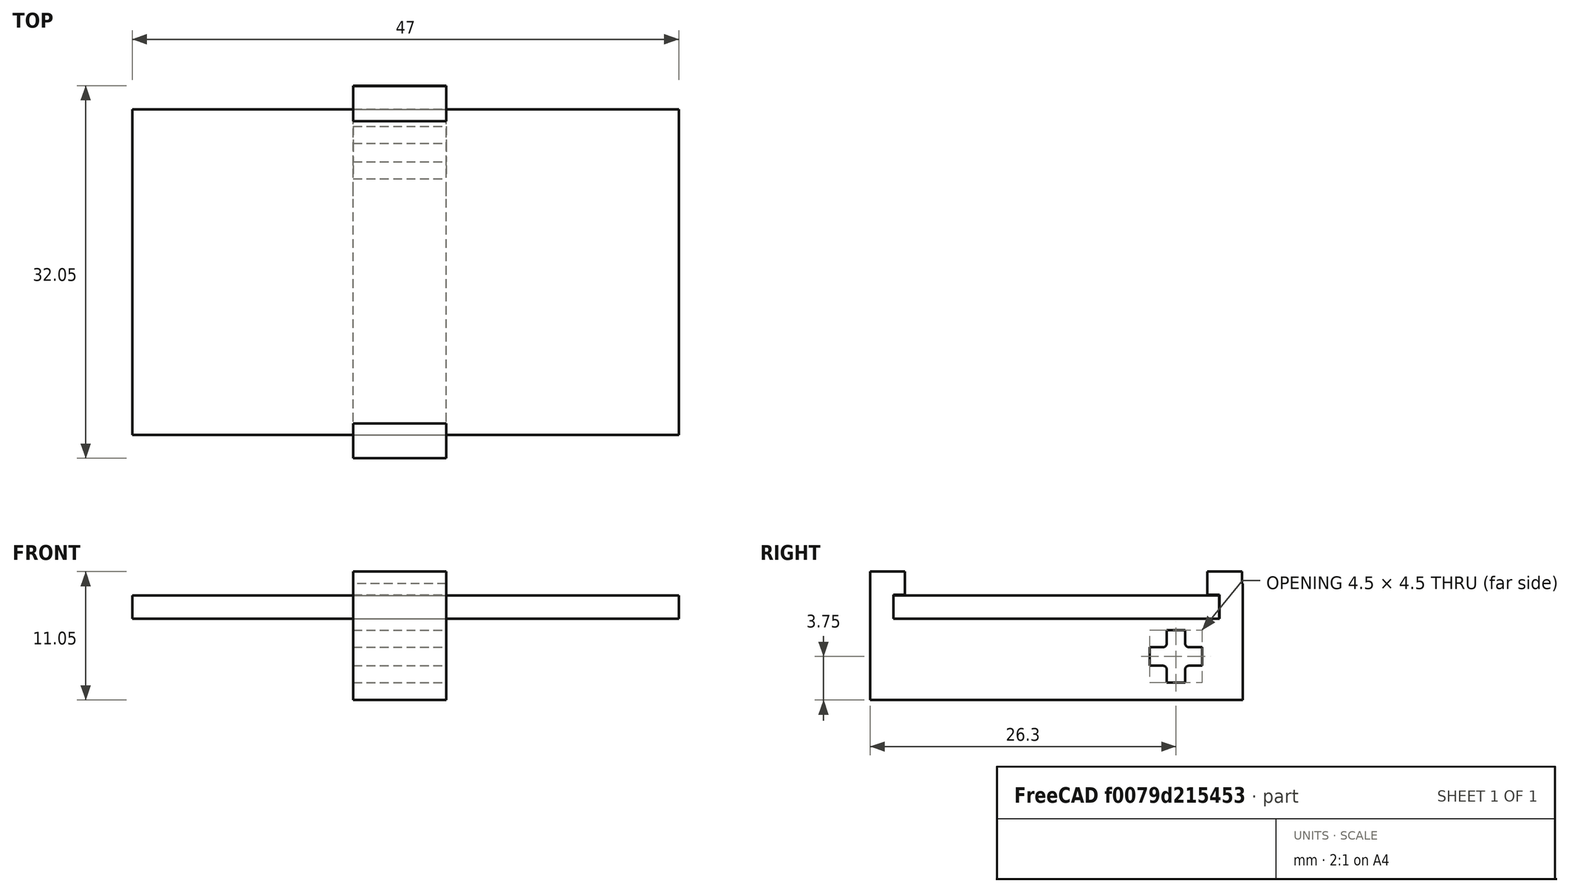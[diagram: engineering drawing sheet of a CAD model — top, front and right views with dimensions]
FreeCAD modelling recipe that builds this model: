
FCSTD DOCUMENT  (FreeCAD 0.20R29177 +426 (Git))
Label: batteryHolder
License: All rights reserved
LicenseURL: http://en.wikipedia.org/wiki/All_rights_reserved
objects: Part::Box×9, Part::MultiFuse×5, Part::Cut×1, Part::Fillet×1
note: 16 computed .brp shape members not serialized (recipe doc carries the construction recipe); baked Part::Feature solids carry a one-line shape summary decoded from their .brp

FEATURE [Part::Box] Box  label="Cube"
  AttacherType = Attacher::AttachEngine3D
  Height = 1.6
  Length = 80
  Placement = pos=(0,-2.25,-0.8) rot=(0,0,1;0rad)
  Width = 4.5
FEATURE [Part::Box] Box001  label="Cube001"
  AttacherType = Attacher::AttachEngine3D
  Height = 1.6
  Length = 80
  Placement = pos=(0,0.8,-2.25) rot=(1,0,0;1.5708rad)
  Width = 4.5
FEATURE [Part::MultiFuse] Fusion
  Placement = pos=(-5,0,0) rot=(0,0,1;0rad)
  Shapes = -> [Box,Box001]
FEATURE [Part::Box] Box002  label="Cube002"
  AttacherType = Attacher::AttachEngine3D
  Height = 7
  Length = 8
  Placement = pos=(0,-3.75,-3.75) rot=(0,0,1;0rad)
  Width = 7.5
FEATURE [Part::Cut] Cut
  Base = -> Box002
  Tool = -> Fusion
FEATURE [Part::Fillet] Fillet
  Base = -> Cut
  Edges = 4 edges r=0.3: [Edge25,Edge30,Edge36,Edge43]
FEATURE [Part::Box] Box003  label="Cube003"
  AttacherType = Attacher::AttachEngine3D
  Height = 10
  Length = 8
  Placement = pos=(0,3.75,-3.75) rot=(0,0,1;0rad)
  Width = 2
FEATURE [Part::Box] Box004  label="bat"
  AttacherType = Attacher::AttachEngine3D
  Height = 2
  Length = 47
  Placement = pos=(-19,-24.3,3.25) rot=(0,0,1;0rad)
  Width = 28
FEATURE [Part::Box] Box005  label="Cube005"
  AttacherType = Attacher::AttachEngine3D
  Height = 2
  Length = 8
  Placement = pos=(0,2.7,5.3) rot=(0,0,1;0rad)
  Width = 3
FEATURE [Part::MultiFuse] Fusion001
  Shapes = -> [Box003,Box005,Fillet]
FEATURE [Part::Box] Box006  label="Cube006"
  AttacherType = Attacher::AttachEngine3D
  Height = 7
  Length = 8
  Placement = pos=(0,-24.3,-3.75) rot=(0,0,1;0rad)
  Width = 21
FEATURE [Part::MultiFuse] Fusion002
  Shapes = -> [Box006,Fusion001]
FEATURE [Part::Box] Box007  label="Cube007"
  AttacherType = Attacher::AttachEngine3D
  Height = 2
  Length = 8
  Placement = pos=(0,-26.3,5.3) rot=(0,0,1;0rad)
  Width = 3
FEATURE [Part::Box] Box008  label="Cube008"
  AttacherType = Attacher::AttachEngine3D
  Height = 10
  Length = 8
  Placement = pos=(0,-26.3,-3.75) rot=(0,0,1;0rad)
  Width = 2
FEATURE [Part::MultiFuse] Fusion003
  Shapes = -> [Box008,Box007]
FEATURE [Part::MultiFuse] Fusion004
  Shapes = -> [Fusion003,Fusion002]
